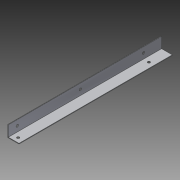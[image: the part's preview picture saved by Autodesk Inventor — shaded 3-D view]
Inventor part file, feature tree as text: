
AUTODESK INVENTOR PART (.ipt)
format: ipt  version: 2014 SP1 (Build 180222100, 222)  size: 99,840 bytes
history: native  units: in
note: dims shown in document units (in); Inventor stores cm internally (conversion verified against a paired STEP export)
features: extrude x3, sketch x3
ambient origin geometry x8: Origin, YZ Plane, XZ Plane, XY Plane, X Axis, Y Axis, Z Axis, Center Point
bodies: Solid1 (feature_tree)
feature tree (6):
  extrude  "Extrusion1"  Depth=0.0312in
  sketch  "Sketch2"  dims[d2=8.5in d3=0.0in d4=1.0in]
  sketch  "Sketch3"  dims[d5=0.135in d6=8.5in d14=0.135in d15=1.0in d16=8.5in d17=1.1811in d19=3.5in d20=0.3937in d22=1.0in d24=1.0in d25=0.0in d26=1.0in d27=0.0in d28=0.25in]
  extrude  "Extrusion2"  Depth=8.5in
  extrude  "Extrusion3"  Depth=8.5in
  sketch  "Sketch1"  dims[d0=0.625in d1=0.0312in]
